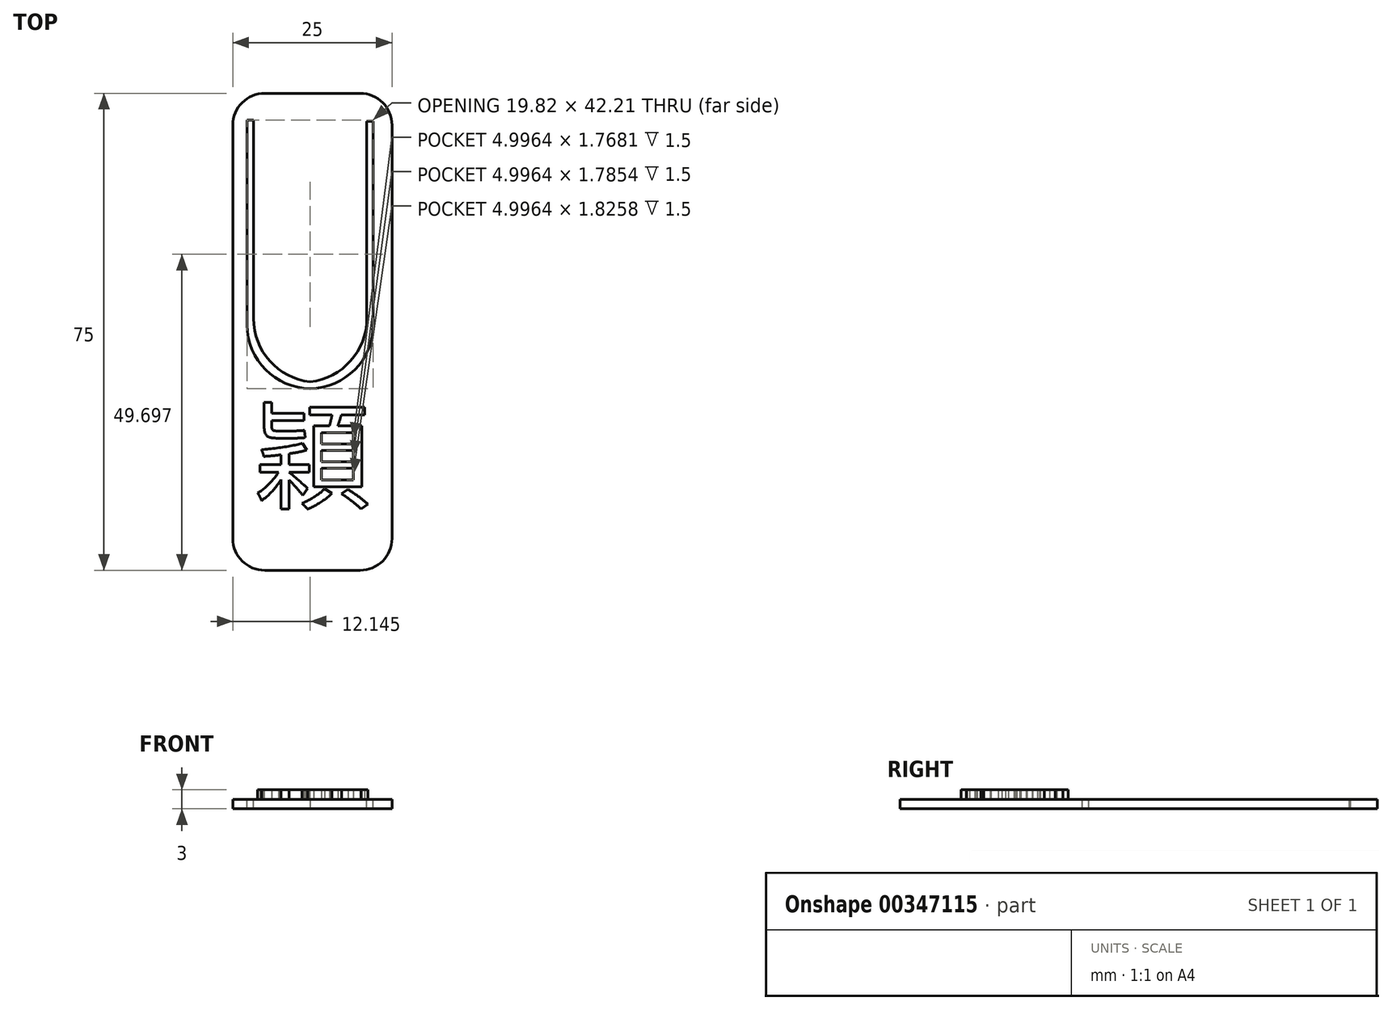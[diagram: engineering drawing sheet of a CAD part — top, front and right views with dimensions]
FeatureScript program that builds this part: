
annotation { "Feature Type Name" : "Feature", "Feature Type Description" : "" }
export const myFeature = defineFeature(function(context is Context, id is Id, definition is map)
    precondition{}
    {
        {
            var Q0;
            Q0=qCreatedBy(makeId("Top.planeOp"),FACE);
            var sketch = newSketch(context, id + "F0", { "sketchPlane" : qUnion([Q0])});
            skLineSegment(sketch, "E0.bottom", {"start": v(-45.14, 36.47) * mm, "end": v(-20.14, 36.47) * mm});
            skLineSegment(sketch, "E0.top", {"start": v(-45.14, -38.53) * mm, "end": v(-20.14, -38.53) * mm});
            skLineSegment(sketch, "E0.left", {"start": v(-45.14, 36.47) * mm, "end": v(-45.14, -38.53) * mm});
            skLineSegment(sketch, "E0.right", {"start": v(-20.14, 36.47) * mm, "end": v(-20.14, -38.53) * mm});
            skSolve(sketch);
        }
        {
            var Q0;
            Q0=makeQuery(id+"F0.imprint","IMPRINT",FACE,{"disambiguationData":[TD([[makeQuery(id+"F0.imprint","IMPRINT",EDGE,{"derivedFrom":sQuery(id+"F0.wireOp",EDGE,"E0.bottom")}),-1.0]])]});
            extrude(context, id + "F1", {"entities" : qUnion([Q0]), "depth" : 1.5 * mm});
        }
        {
            var Q0;
            Q0=makeQuery(id+"F1.opExtrude","CAP_FACE",FACE,{"disambiguationData":[OSD([sQuery(id+"F0.wireOp",EDGE,"E0.bottom"),sQuery(id+"F0.wireOp",EDGE,"E0.top"),sQuery(id+"F0.wireOp",EDGE,"E0.left"),sQuery(id+"F0.wireOp",EDGE,"E0.right")])],"isStart":false});
            var sketch = newSketch(context, id + "F2", { "sketchPlane" : qUnion([Q0])});
            skLineSegment(sketch, "E1", {"start": v(-42.9, 32.27) * mm, "end": v(-42.9, -9.94) * mm});
            skLineSegment(sketch, "E2", {"start": v(-42.9, -9.94) * mm, "end": v(-23.09, -9.94) * mm});
            skLineSegment(sketch, "E3", {"start": v(-23.09, -9.94) * mm, "end": v(-23.09, 32.08) * mm});
            skLineSegment(sketch, "E4.0", {"start": v(-24.09, -8.94) * mm, "end": v(-24.09, 32.08) * mm});
            skLineSegment(sketch, "E4.1", {"start": v(-41.9, -8.94) * mm, "end": v(-24.09, -8.94) * mm});
            skLineSegment(sketch, "E4.2", {"start": v(-41.9, 32.27) * mm, "end": v(-41.9, -8.94) * mm});
            skLineSegment(sketch, "E5", {"start": v(-42.9, 32.27) * mm, "end": v(-41.9, 32.27) * mm});
            skLineSegment(sketch, "E6", {"start": v(-24.09, 32.08) * mm, "end": v(-23.09, 32.08) * mm});
            skSolve(sketch);
        }
        {
            var Q0;
            Q0=makeQuery(id+"F2.imprint","IMPRINT",FACE,{"disambiguationData":[TD([[makeQuery(id+"F2.imprint","IMPRINT",EDGE,{"derivedFrom":sQuery(id+"F2.wireOp",EDGE,"E1")}),1.0]])]});
            extrude(context, id + "F3", {"entities" : qUnion([Q0]), "operationType" : NewBodyOperationType.REMOVE, "oppositeDirection" : true, "depth" : 25 * mm});
        }
        {
            var Q0;
            Q0=makeQuery(id+"F3.boolean.opBoolean","COPY",EDGE,{"derivedFrom":makeQuery(id+"F3.opExtrude","SWEPT_EDGE",EDGE,{"disambiguationData":[OSD([sQuery(id+"F2.wireOp",EDGE,"E4.0"),sQuery(id+"F2.wireOp",EDGE,"E4.1")])]})});
            var Q1;
            Q1=makeQuery(id+"F3.boolean.opBoolean","COPY",EDGE,{"derivedFrom":makeQuery(id+"F3.opExtrude","SWEPT_EDGE",EDGE,{"disambiguationData":[OSD([sQuery(id+"F2.wireOp",EDGE,"E2"),sQuery(id+"F2.wireOp",EDGE,"E3")])]})});
            var Q2;
            Q2=makeQuery(id+"F3.boolean.opBoolean","COPY",EDGE,{"derivedFrom":makeQuery(id+"F3.opExtrude","SWEPT_EDGE",EDGE,{"disambiguationData":[OSD([sQuery(id+"F2.wireOp",EDGE,"E4.1"),sQuery(id+"F2.wireOp",EDGE,"E4.2")])]})});
            var Q3;
            Q3=makeQuery(id+"F3.boolean.opBoolean","COPY",EDGE,{"derivedFrom":makeQuery(id+"F3.opExtrude","SWEPT_EDGE",EDGE,{"disambiguationData":[OSD([sQuery(id+"F2.wireOp",EDGE,"E1"),sQuery(id+"F2.wireOp",EDGE,"E2")])]})});
            fillet(context, id + "F4", {"entities" : qUnion([Q0, Q1, Q2, Q3]), "radius" : 10 * mm, "tangentPropagation" : true, "allowEdgeOverflow" : false});
        }
        {
            var Q0;
            Q0=makeQuery(id+"F1.opExtrude","SWEPT_EDGE",EDGE,{"disambiguationData":[OSD([sQuery(id+"F0.wireOp",EDGE,"E0.bottom"),sQuery(id+"F0.wireOp",EDGE,"E0.left")])]});
            var Q1;
            Q1=makeQuery(id+"F1.opExtrude","SWEPT_EDGE",EDGE,{"disambiguationData":[OSD([sQuery(id+"F0.wireOp",EDGE,"E0.bottom"),sQuery(id+"F0.wireOp",EDGE,"E0.right")])]});
            var Q2;
            Q2=makeQuery(id+"F1.opExtrude","SWEPT_EDGE",EDGE,{"disambiguationData":[OSD([sQuery(id+"F0.wireOp",EDGE,"E0.top"),sQuery(id+"F0.wireOp",EDGE,"E0.left")])]});
            var Q3;
            Q3=makeQuery(id+"F1.opExtrude","SWEPT_EDGE",EDGE,{"disambiguationData":[OSD([sQuery(id+"F0.wireOp",EDGE,"E0.top"),sQuery(id+"F0.wireOp",EDGE,"E0.right")])]});
            fillet(context, id + "F5", {"entities" : qUnion([Q0, Q1, Q2, Q3]), "radius" : 5 * mm, "tangentPropagation" : true, "allowEdgeOverflow" : false});
        }
        {
            var Q0;
            Q0=makeQuery(id+"F1.opExtrude","CAP_FACE",FACE,{"disambiguationData":[OSD([sQuery(id+"F0.wireOp",EDGE,"E0.bottom"),sQuery(id+"F0.wireOp",EDGE,"E0.top"),sQuery(id+"F0.wireOp",EDGE,"E0.left"),sQuery(id+"F0.wireOp",EDGE,"E0.right")])],"isStart":false});
            var sketch = newSketch(context, id + "F6", { "sketchPlane" : qUnion([Q0])});
            skText(sketch, "E7", { "text": "穎\n", "fontName": "NotoSansCJKtc-Regular.otf"});
            const initialGuessF6  = {"E7": [-0.0419, -0.02746, 1, 0, 0.01327]};
            skSetInitialGuess(sketch, initialGuessF6);
            skSolve(sketch);
        }
        {
            var Q0;
            Q0 = qSketchRegion(id + "F6", true);
            extrude(context, id + "F7", {"entities" : qUnion([Q0]), "operationType" : NewBodyOperationType.ADD, "depth" : 1.5 * mm});
        }
    });
